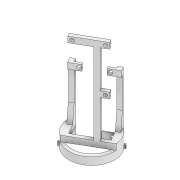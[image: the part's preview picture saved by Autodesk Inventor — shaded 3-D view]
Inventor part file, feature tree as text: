
AUTODESK INVENTOR PART (.ipt)
format: ipt  version: 2022.3 (Build 263350000, 350)  size: 321,536 bytes
history: native  units: mm
features: extrude x12, sketch x12, chamfer x2, other x1, projected_geometry x1
ambient origin geometry x8: Origin, YZ Plane, XZ Plane, XY Plane, X Axis, Y Axis, Z Axis, Center Point
bodies: Body1 (feature_tree)
feature tree (28):
  other  "Sólido1"
  extrude  "Extrusión1"  Depth=0.25mm
  extrude  "Extrusión2"  Depth=1.0mm
  extrude  "Extrusión3"  Depth=6.5mm
  extrude  "Extrusión4"  Depth=2.0mm
  extrude  "Extrusión5"  Depth=2.4mm
  chamfer  "Chaflán1"  Distance=1.0mm
  chamfer  "Chaflán2"  Distance=5.0mm
  extrude  "Extrusión6"  Depth=2.0mm
  extrude  "Extrusión7"  Depth=14.0mm TaperAngle=15.0deg
  extrude  "Extrusión8"  Depth=2.0mm
  extrude  "Extrusión9"  Depth=9.0mm
  extrude  "Extrusión10"  Depth=10.0mm
  extrude  "Extrusión11"  Depth=10.0mm
  extrude  "Extrusión12"  Depth=3.0mm
  sketch  "Boceto1"  dims[d0=39.5mm d1=0.25mm]
  sketch  "Boceto2"  dims[d2=33.5mm d3=1.0mm]
  sketch  "Boceto3"  dims[d4=6.5mm d5=0.0mm d6=39.5mm d7=0.25mm d8=33.5mm d9=1.0mm]
  sketch  "Boceto5"  dims[d10=2.0mm d11=2.0mm]
  sketch  "Boceto7"  dims[d12=2.4mm d13=0.0mm d14=7.0mm]
  sketch  "Boceto8"  dims[d15=3.0mm d16=1.0mm d17=0.0mm]
  sketch  "Boceto9"  dims[d18=18.0mm d19=5.0mm d20=0.0mm]
  sketch  "Boceto10"  dims[d22=3.0mm d23=2.0mm]
  sketch  "Boceto11"  dims[d24=45.0mm d25=0.0mm d26=14.0mm d27=2.0mm d28=15.0deg]
  sketch  "Boceto12"  dims[d29=14.0mm d30=2.0mm d31=15.0deg d32=2.0mm]
  projected_geometry  "Contorno proyectado3"
  sketch  "Boceto13"  dims[d33=9.0mm d34=9.0mm]
  sketch  "Boceto14"  dims[d35=5.0mm d36=0.0mm d37=10.0mm d38=10.0mm d39=3.0mm d40=3.0mm d41=5.0mm d42=0.0mm d43=10.0mm d44=4.0mm d45=75.0mm d46=0.0mm d47=5.0mm d48=6.0mm d49=0.0mm d50=16.5mm d51=0.0mm d52=10.5mm d53=10.5mm d54=3.0mm d55=3.0mm d56=0.0mm d57=0.0mm d58=32.3mm d59=6.0mm d60=5.0mm d61=90.0deg d63=3.0mm d64=0.0mm d65=37.3mm d66=3.0mm]
